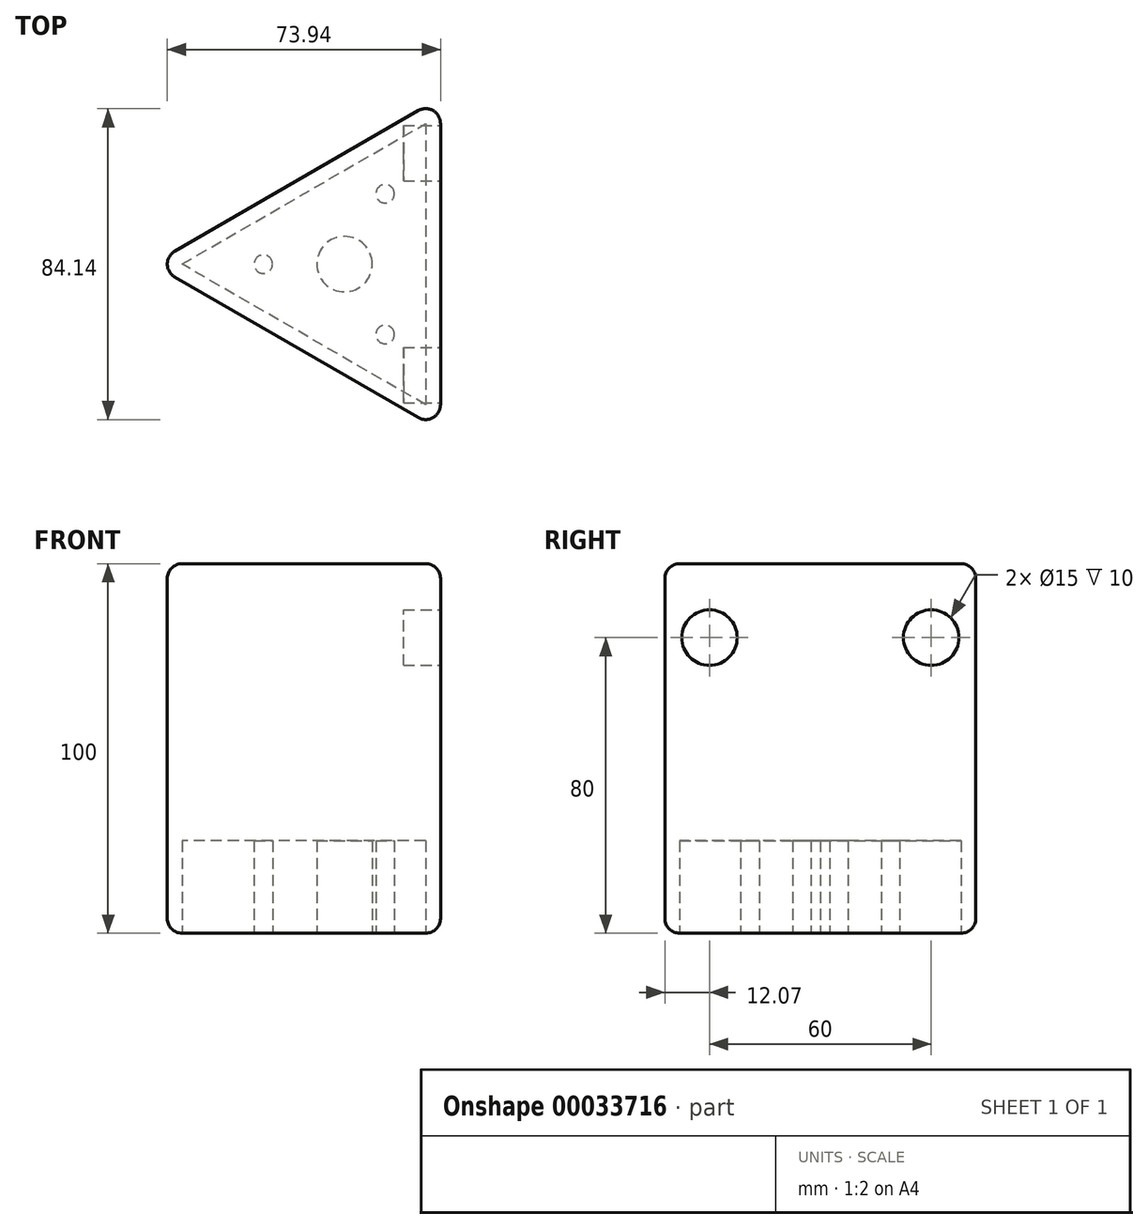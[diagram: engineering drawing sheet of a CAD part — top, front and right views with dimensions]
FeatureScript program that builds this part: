
annotation { "Feature Type Name" : "Feature", "Feature Type Description" : "" }
export const myFeature = defineFeature(function(context is Context, id is Id, definition is map)
    precondition{}
    {
        {
            var Q0;
            Q0=qCreatedBy(makeId("Top.planeOp"),FACE);
            var sketch = newSketch(context, id + "F0", { "sketchPlane" : qUnion([Q0])});
            skCircle(sketch, "E0.cCircle", {"center": v(0, 0) * mm, "radius": 25.98 * mm, "construction": true});
            skLineSegment(sketch, "E0.0", {"start": v(25.98, 45) * mm, "end": v(25.98, -45) * mm});
            skLineSegment(sketch, "E0.1", {"start": v(25.98, -45) * mm, "end": v(-51.96, 0) * mm});
            skLineSegment(sketch, "E0.2", {"start": v(-51.96, 0) * mm, "end": v(25.98, 45) * mm});
            skPoint(sketch, "E0.0.midPoint", {"position": v(25.98, 0) * mm});
            skSolve(sketch);
        }
        {
            var Q0;
            Q0=makeQuery(id+"F0.imprint","IMPRINT",FACE,{"disambiguationData":[TD([[makeQuery(id+"F0.imprint","IMPRINT",EDGE,{"derivedFrom":sQuery(id+"F0.wireOp",EDGE,"E0.0")}),-1.0]])]});
            extrude(context, id + "F1", {"entities" : qUnion([Q0]), "depth" : 100 * mm});
        }
        {
            var Q0;
            Q0=makeQuery(id+"F1.opExtrude","SWEPT_FACE",FACE,{"disambiguationData":[OSD([sQuery(id+"F0.wireOp",EDGE,"E0.0")])]});
            var sketch = newSketch(context, id + "F2", { "sketchPlane" : qUnion([Q0])});
            skPoint(sketch, "E1", {"position": v(-30, 80) * mm});
            skPoint(sketch, "E2", {"position": v(30, 80) * mm});
            skCircle(sketch, "E3", {"center": v(-30, 80) * mm, "radius": 12.5 * mm});
            skCircle(sketch, "E4", {"center": v(30, 80) * mm, "radius": 12.5 * mm});
            skCircle(sketch, "E5", {"center": v(-30, 80) * mm, "radius": 7.5 * mm});
            skCircle(sketch, "E6", {"center": v(30, 80) * mm, "radius": 7.5 * mm});
            skSolve(sketch);
        }
        {
            var Q0;
            Q0=makeQuery(id+"F2.imprint","IMPRINT",FACE,{"disambiguationData":[TD([[makeQuery(id+"F2.imprint","IMPRINT",EDGE,{"derivedFrom":sQuery(id+"F2.wireOp",EDGE,"E5")}),1.0]])]});
            var Q1;
            Q1=makeQuery(id+"F2.imprint","IMPRINT",FACE,{"disambiguationData":[TD([[makeQuery(id+"F2.imprint","IMPRINT",EDGE,{"derivedFrom":sQuery(id+"F2.wireOp",EDGE,"E6")}),1.0]])]});
            extrude(context, id + "F3", {"entities" : qUnion([Q0, Q1]), "operationType" : NewBodyOperationType.REMOVE, "oppositeDirection" : true, "depth" : 10 * mm});
        }
        {
            var Q0;
            Q0=makeQuery(id+"F1.opExtrude","SWEPT_EDGE",EDGE,{"disambiguationData":[OSD([sQuery(id+"F0.wireOp",EDGE,"E0.0"),sQuery(id+"F0.wireOp",EDGE,"E0.1")])]});
            var Q1;
            Q1=makeQuery(id+"F1.opExtrude","SWEPT_EDGE",EDGE,{"disambiguationData":[OSD([sQuery(id+"F0.wireOp",EDGE,"E0.0"),sQuery(id+"F0.wireOp",EDGE,"E0.2")])]});
            var Q2;
            Q2=makeQuery(id+"F1.opExtrude","SWEPT_EDGE",EDGE,{"disambiguationData":[OSD([sQuery(id+"F0.wireOp",EDGE,"E0.1"),sQuery(id+"F0.wireOp",EDGE,"E0.2")])]});
            var Q3;
            Q3=makeQuery(id+"F1.opExtrude","CAP_EDGE",EDGE,{"disambiguationData":[OSD([sQuery(id+"F0.wireOp",EDGE,"E0.1")])],"isStart":false});
            var Q4;
            Q4=makeQuery(id+"F1.opExtrude","CAP_EDGE",EDGE,{"disambiguationData":[OSD([sQuery(id+"F0.wireOp",EDGE,"E0.2")])],"isStart":false});
            var Q5;
            Q5=makeQuery(id+"F1.opExtrude","CAP_EDGE",EDGE,{"disambiguationData":[OSD([sQuery(id+"F0.wireOp",EDGE,"E0.0")])],"isStart":false});
            var Q6;
            Q6=makeQuery(id+"F1.opExtrude","CAP_EDGE",EDGE,{"disambiguationData":[OSD([sQuery(id+"F0.wireOp",EDGE,"E0.1")])],"isStart":true});
            var Q7;
            Q7=makeQuery(id+"F1.opExtrude","CAP_EDGE",EDGE,{"disambiguationData":[OSD([sQuery(id+"F0.wireOp",EDGE,"E0.0")])],"isStart":true});
            var Q8;
            Q8=makeQuery(id+"F1.opExtrude","CAP_EDGE",EDGE,{"disambiguationData":[OSD([sQuery(id+"F0.wireOp",EDGE,"E0.2")])],"isStart":true});
            fillet(context, id + "F4", {"entities" : qUnion([Q0, Q1, Q2, Q3, Q4, Q5, Q6, Q7, Q8]), "radius" : 4 * mm, "tangentPropagation" : true, "allowEdgeOverflow" : false});
        }
        {
            var Q0;
            Q0=makeQuery(id+"F1.opExtrude","CAP_FACE",FACE,{"disambiguationData":[OSD([sQuery(id+"F0.wireOp",EDGE,"E0.0"),sQuery(id+"F0.wireOp",EDGE,"E0.1"),sQuery(id+"F0.wireOp",EDGE,"E0.2")])],"isStart":true});
            var sketch = newSketch(context, id + "F5", { "sketchPlane" : qUnion([Q0])});
            skCircle(sketch, "E7", {"center": v(0, 0) * mm, "radius": 7.5 * mm});
            skLineSegment(sketch, "E8", {"start": v(0, 0) * mm, "end": v(21.98, 38.07) * mm});
            skLineSegment(sketch, "E9", {"start": v(21.98, 38.07) * mm, "end": v(0, 0) * mm});
            skLineSegment(sketch, "E10", {"start": v(21.98, -38.07) * mm, "end": v(0, 0) * mm});
            skLineSegment(sketch, "E11", {"start": v(0, 0) * mm, "end": v(-43.96, 0) * mm});
            skPoint(sketch, "E12", {"position": v(-21.98, 0) * mm});
            skPoint(sketch, "E13", {"position": v(11, 19.04) * mm});
            skPoint(sketch, "E14", {"position": v(11, -19.04) * mm});
            skCircle(sketch, "E15", {"center": v(-21.98, 0) * mm, "radius": 2.5 * mm});
            skCircle(sketch, "E16", {"center": v(11, 19.04) * mm, "radius": 2.5 * mm});
            skCircle(sketch, "E17", {"center": v(11, -19.04) * mm, "radius": 2.5 * mm});
            skSolve(sketch);
        }
        {
            var Q0;
            {var subQ0=sQuery(id+"F5.wireOp",EDGE,"E17");var subQ1=sQuery(id+"F5.wireOp",EDGE,"E10");var subQ3=makeQuery(id+"F5.imprint","INTERSECT",VERTEX,{"disambiguationData":[OD(0.0)],"derivedFrom":[subQ1,subQ0]});Q0=makeQuery(id+"F5.imprint","IMPRINT",FACE,{"disambiguationData":[TD([[makeQuery(id+"F5.imprint","IMPRINT",EDGE,{"disambiguationData":[TD([[subQ3,-1.0]])],"derivedFrom":subQ1}),1.0]])]});}
            var Q1;
            {var subQ0=sQuery(id+"F5.wireOp",EDGE,"E17");var subQ1=sQuery(id+"F5.wireOp",EDGE,"E10");var subQ3=makeQuery(id+"F5.imprint","INTERSECT",VERTEX,{"disambiguationData":[OD(0.0)],"derivedFrom":[subQ1,subQ0]});Q1=makeQuery(id+"F5.imprint","IMPRINT",FACE,{"disambiguationData":[TD([[makeQuery(id+"F5.imprint","IMPRINT",EDGE,{"disambiguationData":[TD([[subQ3,-1.0]])],"derivedFrom":subQ1}),-1.0]])]});}
            var Q2;
            {var subQ0=sQuery(id+"F5.wireOp",EDGE,"E15");var subQ1=sQuery(id+"F5.wireOp",EDGE,"E11");var subQ3=makeQuery(id+"F5.imprint","INTERSECT",VERTEX,{"disambiguationData":[OD(0.0)],"derivedFrom":[subQ1,subQ0]});Q2=makeQuery(id+"F5.imprint","IMPRINT",FACE,{"disambiguationData":[TD([[makeQuery(id+"F5.imprint","IMPRINT",EDGE,{"disambiguationData":[TD([[subQ3,-1.0]])],"derivedFrom":subQ1}),1.0]])]});}
            var Q3;
            {var subQ0=sQuery(id+"F5.wireOp",EDGE,"E15");var subQ1=sQuery(id+"F5.wireOp",EDGE,"E11");var subQ3=makeQuery(id+"F5.imprint","INTERSECT",VERTEX,{"disambiguationData":[OD(0.0)],"derivedFrom":[subQ1,subQ0]});Q3=makeQuery(id+"F5.imprint","IMPRINT",FACE,{"disambiguationData":[TD([[makeQuery(id+"F5.imprint","IMPRINT",EDGE,{"disambiguationData":[TD([[subQ3,-1.0]])],"derivedFrom":subQ1}),-1.0]])]});}
            var Q4;
            {var subQ0=sQuery(id+"F5.wireOp",EDGE,"E16");var subQ1=sQuery(id+"F5.wireOp",EDGE,"E9");var subQ3=makeQuery(id+"F5.imprint","INTERSECT",VERTEX,{"disambiguationData":[OD(0.0)],"derivedFrom":[subQ1,subQ0]});Q4=makeQuery(id+"F5.imprint","IMPRINT",FACE,{"disambiguationData":[TD([[makeQuery(id+"F5.imprint","IMPRINT",EDGE,{"disambiguationData":[TD([[subQ3,-1.0]])],"derivedFrom":subQ1}),1.0]])]});}
            var Q5;
            {var subQ0=sQuery(id+"F5.wireOp",EDGE,"E16");var subQ1=sQuery(id+"F5.wireOp",EDGE,"E9");var subQ3=makeQuery(id+"F5.imprint","INTERSECT",VERTEX,{"disambiguationData":[OD(0.0)],"derivedFrom":[subQ1,subQ0]});Q5=makeQuery(id+"F5.imprint","IMPRINT",FACE,{"disambiguationData":[TD([[makeQuery(id+"F5.imprint","IMPRINT",EDGE,{"disambiguationData":[TD([[subQ3,-1.0]])],"derivedFrom":subQ1}),-1.0]])]});}
            extrude(context, id + "F6", {"entities" : qUnion([Q0, Q1, Q2, Q3, Q4, Q5]), "operationType" : NewBodyOperationType.REMOVE, "oppositeDirection" : true, "depth" : 25 * mm});
        }
    });
